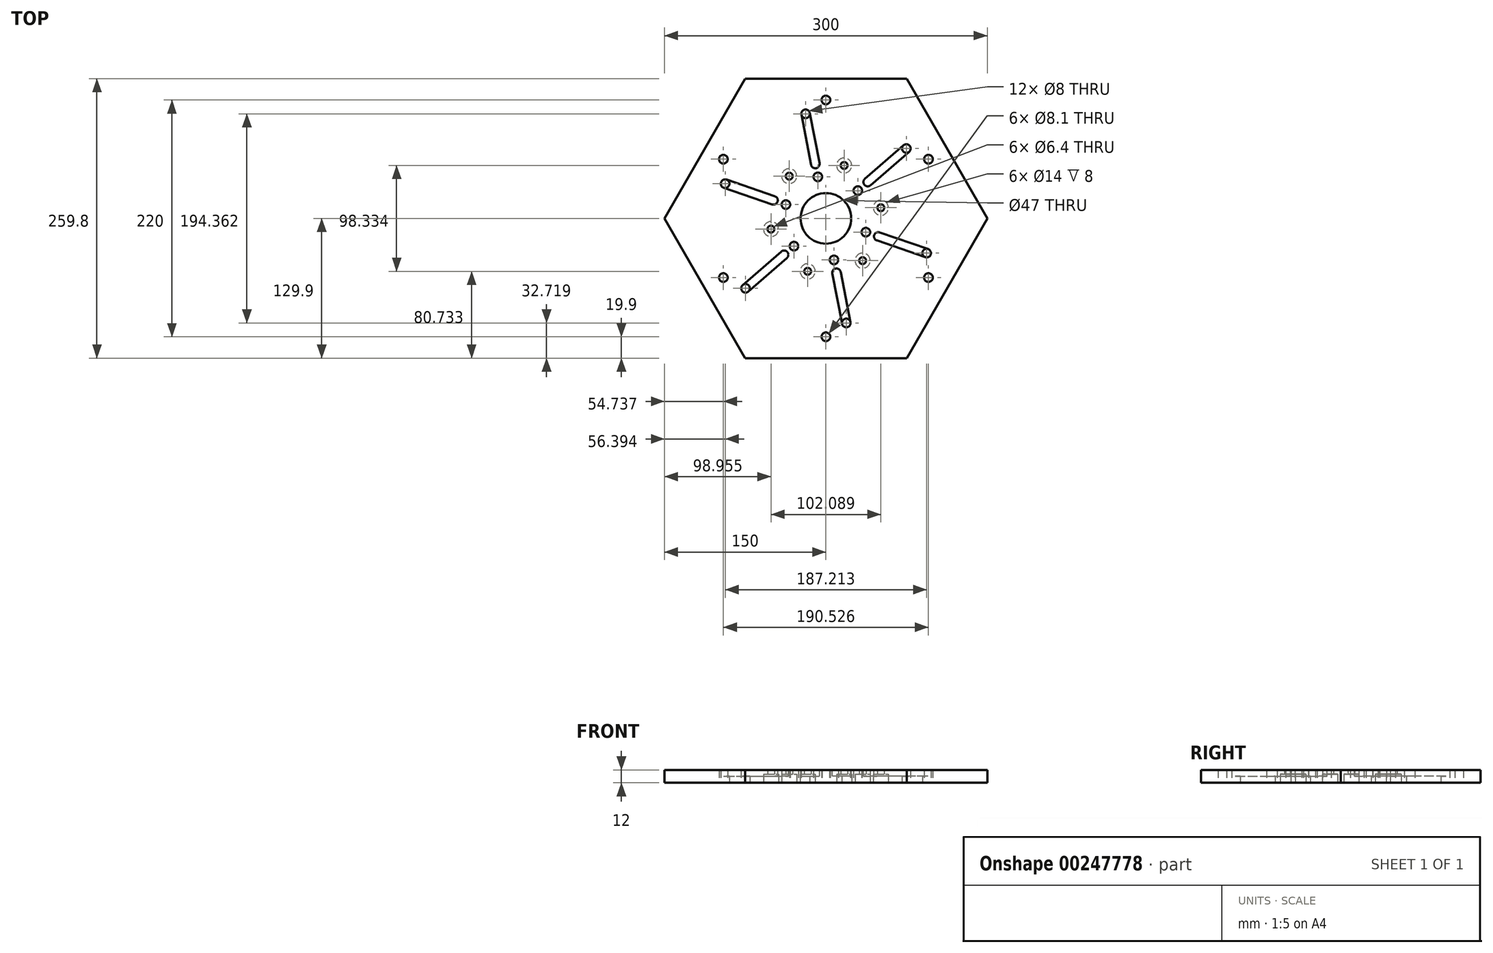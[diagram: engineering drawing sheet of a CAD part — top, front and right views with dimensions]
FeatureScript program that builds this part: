
annotation { "Feature Type Name" : "Feature", "Feature Type Description" : "" }
export const myFeature = defineFeature(function(context is Context, id is Id, definition is map)
    precondition{}
    {
        {
            var Q0;
            Q0=qCreatedBy(makeId("Top.planeOp"),FACE);
            var sketch = newSketch(context, id + "F0", { "sketchPlane" : qUnion([Q0])});
            skCircle(sketch, "E0.cCircle", {"center": v(0, 0) * mm, "radius": 150 * mm, "construction": true});
            skLineSegment(sketch, "E0.0", {"start": v(-150, 0) * mm, "end": v(-75, 129.9) * mm});
            skLineSegment(sketch, "E0.1", {"start": v(-75, 129.9) * mm, "end": v(75, 129.9) * mm});
            skLineSegment(sketch, "E0.2", {"start": v(75, 129.9) * mm, "end": v(150, 0) * mm});
            skLineSegment(sketch, "E0.3", {"start": v(150, 0) * mm, "end": v(75, -129.9) * mm});
            skLineSegment(sketch, "E0.4", {"start": v(75, -129.9) * mm, "end": v(-75, -129.9) * mm});
            skLineSegment(sketch, "E0.5", {"start": v(-75, -129.9) * mm, "end": v(-150, 0) * mm});
            skLineSegment(sketch, "E1", {"start": v(-125.66, 72.55) * mm, "end": v(0, 0) * mm, "construction": true});
            skLineSegment(sketch, "E2", {"start": v(-114.43, 89.16) * mm, "end": v(24.62, 8.88) * mm, "construction": true});
            skCircle(sketch, "E3", {"center": v(0, 0) * mm, "radius": 110 * mm, "construction": true});
            skLineSegment(sketch, "E4", {"start": v(-120.9, 10.58) * mm, "end": v(-58.23, 119.14) * mm, "construction": true});
            skCircle(sketch, "E5", {"center": v(0, 0) * mm, "radius": 95 * mm, "construction": true});
            skCircle(sketch, "E6", {"center": v(0, 0) * mm, "radius": 99 * mm, "construction": true});
            skLineSegment(sketch, "E7", {"start": v(-18.9, 97.18) * mm, "end": v(0, 0) * mm, "construction": true});
            skCircle(sketch, "E8", {"center": v(-18.9, 97.18) * mm, "radius": 4 * mm});
            skCircle(sketch, "E9", {"center": v(0, 0) * mm, "radius": 12 * mm});
            skCircle(sketch, "E10.1.0", {"center": v(-93.6, 32.23) * mm, "radius": 4 * mm});
            skCircle(sketch, "E10.2.0", {"center": v(-74.72, -64.95) * mm, "radius": 4 * mm});
            skCircle(sketch, "E10.3.0", {"center": v(18.9, -97.18) * mm, "radius": 4 * mm});
            skCircle(sketch, "E10.4.0", {"center": v(93.6, -32.23) * mm, "radius": 4 * mm});
            skCircle(sketch, "E10.5.0", {"center": v(74.72, 64.95) * mm, "radius": 4 * mm});
            skCircle(sketch, "E11", {"center": v(-85.26, 72.32) * mm, "radius": 65 * mm, "construction": true});
            skCircle(sketch, "E12", {"center": v(0, 0) * mm, "radius": 39.3 * mm, "construction": true});
            skCircle(sketch, "E13", {"center": v(-7.5, 38.58) * mm, "radius": 4 * mm});
            skCircle(sketch, "E14.1.0", {"center": v(-37.16, 12.8) * mm, "radius": 4 * mm});
            skCircle(sketch, "E14.2.0", {"center": v(-29.66, -25.78) * mm, "radius": 4 * mm});
            skCircle(sketch, "E14.3.0", {"center": v(7.5, -38.58) * mm, "radius": 4 * mm});
            skCircle(sketch, "E14.4.0", {"center": v(37.16, -12.8) * mm, "radius": 4 * mm});
            skCircle(sketch, "E14.5.0", {"center": v(29.66, 25.78) * mm, "radius": 4 * mm});
            skCircle(sketch, "E15", {"center": v(0, 110) * mm, "radius": 4.05 * mm});
            skCircle(sketch, "E16.1.0", {"center": v(-95.26, 55) * mm, "radius": 4.05 * mm});
            skCircle(sketch, "E16.2.0", {"center": v(-95.26, -55) * mm, "radius": 4.05 * mm});
            skCircle(sketch, "E16.3.0", {"center": v(0, -110) * mm, "radius": 4.05 * mm});
            skCircle(sketch, "E16.4.0", {"center": v(95.26, -55) * mm, "radius": 4.05 * mm});
            skCircle(sketch, "E16.5.0", {"center": v(95.26, 55) * mm, "radius": 4.05 * mm});
            skSolve(sketch);
        }
        {
            var Q0;
            Q0=makeQuery(id+"F0.imprint","IMPRINT",FACE,{"disambiguationData":[TD([[makeQuery(id+"F0.imprint","IMPRINT",EDGE,{"derivedFrom":sQuery(id+"F0.wireOp",EDGE,"E0.0")}),-1.0]])]});
            extrude(context, id + "F1", {"entities" : qUnion([Q0]), "depth" : 12 * mm});
        }
        {
            var Q0;
            Q0=makeQuery(id+"F0.imprint","IMPRINT",FACE,{"disambiguationData":[TD([[makeQuery(id+"F0.imprint","IMPRINT",EDGE,{"derivedFrom":sQuery(id+"F0.wireOp",EDGE,"E0.0")}),-1.0]])]});
            var sketch = newSketch(context, id + "F2", { "sketchPlane" : qUnion([Q0])});
            skCircle(sketch, "E17", {"center": v(0, 0) * mm, "radius": 23.5 * mm});
            skSolve(sketch);
        }
        {
            var Q0;
            Q0=qSketchRegion(id+"F2",true);
            extrude(context, id + "F3", {"entities" : qUnion([Q0]), "operationType" : NewBodyOperationType.REMOVE, "depth" : 12 * mm});
        }
        {
            var Q0;
            Q0=makeQuery(id+"F1.opExtrude","CAP_FACE",FACE,{"disambiguationData":[OSD([sQuery(id+"F0.wireOp",EDGE,"E0.0"),sQuery(id+"F0.wireOp",EDGE,"E0.1"),sQuery(id+"F0.wireOp",EDGE,"E0.2"),sQuery(id+"F0.wireOp",EDGE,"E0.3"),sQuery(id+"F0.wireOp",EDGE,"E0.4"),sQuery(id+"F0.wireOp",EDGE,"E0.5"),sQuery(id+"F0.wireOp",EDGE,"E8"),sQuery(id+"F0.wireOp",EDGE,"E9"),sQuery(id+"F0.wireOp",EDGE,"E10.1.0"),sQuery(id+"F0.wireOp",EDGE,"E10.2.0"),sQuery(id+"F0.wireOp",EDGE,"E10.3.0"),sQuery(id+"F0.wireOp",EDGE,"E10.4.0"),sQuery(id+"F0.wireOp",EDGE,"E10.5.0")])],"isStart":false});
            var sketch = newSketch(context, id + "F4", { "sketchPlane" : qUnion([Q0])});
            skLineSegment(sketch, "E18.0", {"start": v(-150, 0) * mm, "end": v(-75, 129.9) * mm});
            skLineSegment(sketch, "E19.0", {"start": v(-22.36, 115.01) * mm, "end": v(0, 0) * mm, "construction": true});
            skArc(sketch, "E20", {"start": v(-14.96, 97.94) * mm, "mid": v(-19.65, 101.1) * mm, "end": v(-22.82, 96.42) * mm});
            skLineSegment(sketch, "E21", {"start": v(-22.82, 96.42) * mm, "end": v(-13.75, 49.8) * mm});
            skLineSegment(sketch, "E22.MirrorCS", {"start": v(-14.96, 97.94) * mm, "end": v(-5.9, 51.32) * mm});
            skArc(sketch, "E23", {"start": v(-13.75, 49.8) * mm, "mid": v(-9.06, 46.63) * mm, "end": v(-5.9, 51.32) * mm});
            skPoint(sketch, "E24.center", {"position": v(0, 0) * mm});
            skCircle(sketch, "E25", {"center": v(0, 0) * mm, "radius": 51.5 * mm, "construction": true});
            skCircle(sketch, "E26", {"center": v(0, 0) * mm, "radius": 99 * mm, "construction": true});
            skSolve(sketch);
        }
        {
            var Q0;
            Q0=qSketchRegion(id+"F4",true);
            extrude(context, id + "F5", {"entities" : qUnion([Q0]), "oppositeDirection" : true, "depth" : 6 * mm, "hasSecondDirection" : true, "secondDirectionOppositeDirection" : false, "secondDirectionDepth" : 10 * mm});
        }
        {
            var Q0;
            Q0=makeQuery(id+"F5.opExtrude","SWEPT_BODY",BODY,{"disambiguationData":[OSD([sQuery(id+"F4.wireOp",EDGE,"E20"),sQuery(id+"F4.wireOp",EDGE,"E21"),sQuery(id+"F4.wireOp",EDGE,"E22.MirrorCS"),sQuery(id+"F4.wireOp",EDGE,"E23")])]});
            var Q1;
            Q1=makeQuery(id+"F3.boolean.opBoolean","COPY",FACE,{"derivedFrom":makeQuery(id+"F3.opExtrude","SWEPT_FACE",FACE,{"disambiguationData":[OSD([sQuery(id+"F2.wireOp",EDGE,"E17")])]})});
            circularPattern(context, id + "F6", {"operationType" : NewBodyOperationType.REMOVE, "entities" : qUnion([Q0]), "axis" : qUnion([Q1]), "angle" : 360 * degree, "instanceCount" : 6, "equalSpace" : true});
        }
        {
            var Q0;
            Q0=makeQuery(id+"F1.opExtrude","CAP_FACE",FACE,{"disambiguationData":[OSD([sQuery(id+"F0.wireOp",EDGE,"E0.0"),sQuery(id+"F0.wireOp",EDGE,"E0.1"),sQuery(id+"F0.wireOp",EDGE,"E0.2"),sQuery(id+"F0.wireOp",EDGE,"E0.3"),sQuery(id+"F0.wireOp",EDGE,"E0.4"),sQuery(id+"F0.wireOp",EDGE,"E0.5"),sQuery(id+"F0.wireOp",EDGE,"E8"),sQuery(id+"F0.wireOp",EDGE,"E9"),sQuery(id+"F0.wireOp",EDGE,"E10.1.0"),sQuery(id+"F0.wireOp",EDGE,"E10.2.0"),sQuery(id+"F0.wireOp",EDGE,"E10.3.0"),sQuery(id+"F0.wireOp",EDGE,"E10.4.0"),sQuery(id+"F0.wireOp",EDGE,"E10.5.0"),sQuery(id+"F0.wireOp",EDGE,"E13"),sQuery(id+"F0.wireOp",EDGE,"E14.1.0"),sQuery(id+"F0.wireOp",EDGE,"E14.2.0"),sQuery(id+"F0.wireOp",EDGE,"E14.3.0"),sQuery(id+"F0.wireOp",EDGE,"E14.4.0"),sQuery(id+"F0.wireOp",EDGE,"E14.5.0"),sQuery(id+"F0.wireOp",EDGE,"E15"),sQuery(id+"F0.wireOp",EDGE,"E16.1.0"),sQuery(id+"F0.wireOp",EDGE,"E16.2.0"),sQuery(id+"F0.wireOp",EDGE,"E16.3.0"),sQuery(id+"F0.wireOp",EDGE,"E16.4.0"),sQuery(id+"F0.wireOp",EDGE,"E16.5.0")])],"isStart":true});
            var sketch = newSketch(context, id + "F7", { "sketchPlane" : qUnion([Q0])});
            skLineSegment(sketch, "E27", {"start": v(0, 0) * mm, "end": v(-22.59, 65.6) * mm, "construction": true});
            skCircle(sketch, "E28", {"center": v(0, 0) * mm, "radius": 52 * mm, "construction": true});
            skPoint(sketch, "E29", {"position": v(-16.93, 49.17) * mm});
            skPoint(sketch, "E30.1.0", {"position": v(-51.04, 9.92) * mm});
            skPoint(sketch, "E30.2.0", {"position": v(-34.12, -39.24) * mm});
            skPoint(sketch, "E31.0.3.0", {"position": v(16.93, -49.17) * mm});
            skPoint(sketch, "E31.0.4.0", {"position": v(51.04, -9.92) * mm});
            skPoint(sketch, "E31.0.5.0", {"position": v(34.12, 39.24) * mm});
            skSolve(sketch);
        }
        {
            var Q0;
            Q0=sQuery(id+"F7.wireOp",VERTEX,"E29");
            var Q1;
            Q1=sQuery(id+"F7.wireOp",VERTEX,"E30.1.0");
            var Q2;
            Q2=sQuery(id+"F7.wireOp",VERTEX,"E30.2.0");
            var Q3;
            Q3=sQuery(id+"F7.wireOp",VERTEX,"E31.0.3.0");
            var Q4;
            Q4=sQuery(id+"F7.wireOp",VERTEX,"E31.0.4.0");
            var Q5;
            Q5=sQuery(id+"F7.wireOp",VERTEX,"E31.0.5.0");
            var Q6;
            Q6=makeQuery(id+"F1.opExtrude","SWEPT_BODY",BODY,{"disambiguationData":[OSD([sQuery(id+"F0.wireOp",EDGE,"E0.0"),sQuery(id+"F0.wireOp",EDGE,"E0.1"),sQuery(id+"F0.wireOp",EDGE,"E0.2"),sQuery(id+"F0.wireOp",EDGE,"E0.3"),sQuery(id+"F0.wireOp",EDGE,"E0.4"),sQuery(id+"F0.wireOp",EDGE,"E0.5"),sQuery(id+"F0.wireOp",EDGE,"E8"),sQuery(id+"F0.wireOp",EDGE,"E9"),sQuery(id+"F0.wireOp",EDGE,"E10.1.0"),sQuery(id+"F0.wireOp",EDGE,"E10.2.0"),sQuery(id+"F0.wireOp",EDGE,"E10.3.0"),sQuery(id+"F0.wireOp",EDGE,"E10.4.0"),sQuery(id+"F0.wireOp",EDGE,"E10.5.0"),sQuery(id+"F0.wireOp",EDGE,"E13"),sQuery(id+"F0.wireOp",EDGE,"E14.1.0"),sQuery(id+"F0.wireOp",EDGE,"E14.2.0"),sQuery(id+"F0.wireOp",EDGE,"E14.3.0"),sQuery(id+"F0.wireOp",EDGE,"E14.4.0"),sQuery(id+"F0.wireOp",EDGE,"E14.5.0"),sQuery(id+"F0.wireOp",EDGE,"E15"),sQuery(id+"F0.wireOp",EDGE,"E16.1.0"),sQuery(id+"F0.wireOp",EDGE,"E16.2.0"),sQuery(id+"F0.wireOp",EDGE,"E16.3.0"),sQuery(id+"F0.wireOp",EDGE,"E16.4.0"),sQuery(id+"F0.wireOp",EDGE,"E16.5.0")])]});
            hole(context, id + "F8", {"style" : HoleStyle.C_BORE, "endStyle" : HoleEndStyle.BLIND, "holeDiameter" : 6.4 * mm, "cBoreDiameter" : 14 * mm, "cBoreDepth" : 8 * mm, "holeDepth" : 20 * mm, "locations" : qUnion([Q0, Q1, Q2, Q3, Q4, Q5]), "scope" : qUnion([Q6])});
        }
    });
